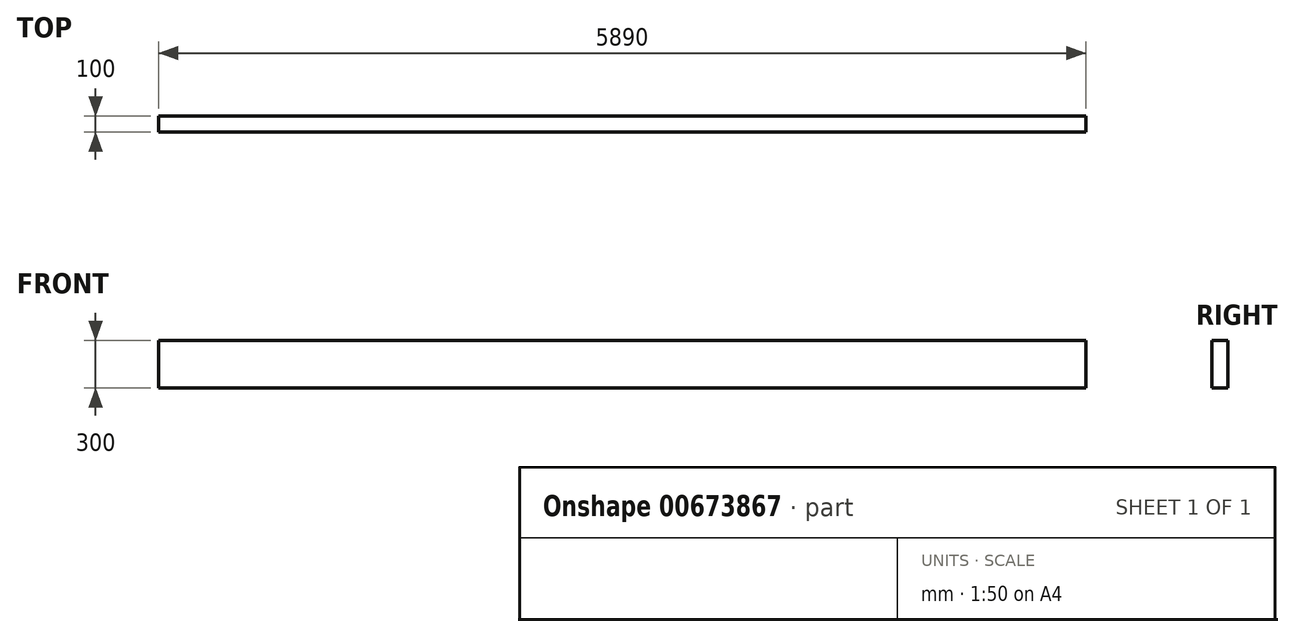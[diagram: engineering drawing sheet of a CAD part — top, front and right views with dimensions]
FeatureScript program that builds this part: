
annotation { "Feature Type Name" : "Feature", "Feature Type Description" : "" }
export const myFeature = defineFeature(function(context is Context, id is Id, definition is map)
    precondition{}
    {
        {
            var Q0;
            Q0=qCreatedBy(makeId("Front.planeOp"),FACE);
            var sketch = newSketch(context, id + "F0", { "sketchPlane" : qUnion([Q0])});
            skLineSegment(sketch, "E0.bottom", {"start": v(0, 0) * mm, "end": v(5890, 0) * mm});
            skLineSegment(sketch, "E0.top", {"start": v(0, -300) * mm, "end": v(5890, -300) * mm});
            skLineSegment(sketch, "E0.left", {"start": v(0, 0) * mm, "end": v(0, -300) * mm});
            skLineSegment(sketch, "E0.right", {"start": v(5890, 0) * mm, "end": v(5890, -300) * mm});
            skSolve(sketch);
        }
        {
            var Q0;
            Q0 = qSketchRegion(id + "F0", true);
            extrude(context, id + "F1", {"entities" : qUnion([Q0]), "depth" : 100 * mm, "offsetDistance" : 25 * mm});
        }
    });
